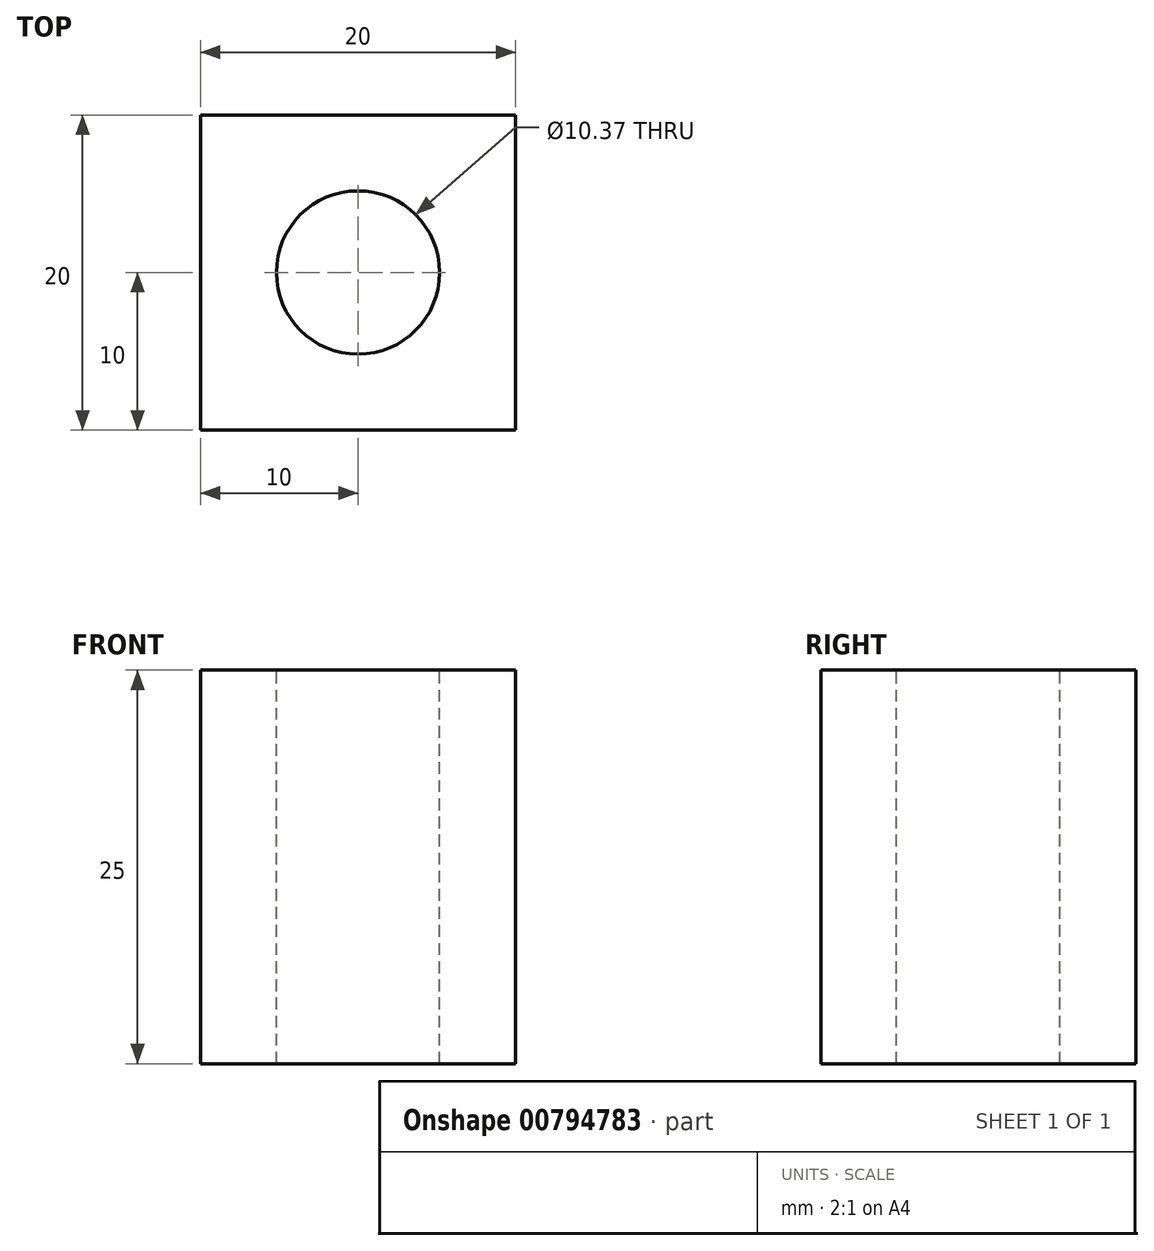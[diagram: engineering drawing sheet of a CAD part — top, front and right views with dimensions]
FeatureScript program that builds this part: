
annotation { "Feature Type Name" : "Feature", "Feature Type Description" : "" }
export const myFeature = defineFeature(function(context is Context, id is Id, definition is map)
    precondition{}
    {
        {
            var Q0;
            Q0=qCreatedBy(makeId("Top.planeOp"),FACE);
            var sketch = newSketch(context, id + "F0", { "sketchPlane" : qUnion([Q0])});
            skLineSegment(sketch, "E0.bottom", {"start": v(10, -10) * mm, "end": v(-10, -10) * mm});
            skLineSegment(sketch, "E0.top", {"start": v(10, 10) * mm, "end": v(-10, 10) * mm});
            skLineSegment(sketch, "E0.left", {"start": v(10, -10) * mm, "end": v(10, 10) * mm});
            skLineSegment(sketch, "E0.right", {"start": v(-10, -10) * mm, "end": v(-10, 10) * mm});
            skPoint(sketch, "E0.middle", {"position": v(0, 0) * mm});
            skSolve(sketch);
        }
        {
            var Q0;
            Q0 = qSketchRegion(id + "F0", true);
            extrude(context, id + "F1", {"entities" : qUnion([Q0]), "depth" : 25 * mm, "offsetDistance" : 25 * mm});
        }
        {
            var Q0;
            Q0=makeQuery(id+"F1.opExtrude","CAP_FACE",FACE,{"disambiguationData":[OSD([sQuery(id+"F0.wireOp",EDGE,"E0.bottom"),sQuery(id+"F0.wireOp",EDGE,"E0.top"),sQuery(id+"F0.wireOp",EDGE,"E0.left"),sQuery(id+"F0.wireOp",EDGE,"E0.right")])],"isStart":false});
            var sketch = newSketch(context, id + "F2", { "sketchPlane" : qUnion([Q0])});
            skSolve(sketch);
        }
        {
            var Q0;
            Q0=makeQuery(id+"F2.imprint","IMPRINT",FACE,{"disambiguationData":[TD([[makeQuery(id+"F2.imprint","IMPRINT",EDGE,{"derivedFrom":makeQuery(id+"F1.opExtrude","CAP_EDGE",EDGE,{"disambiguationData":[OSD([sQuery(id+"F0.wireOp",EDGE,"E0.bottom")])],"isStart":false})}),-1.0]])]});
            cPlane(context, id + "F3", {"entities" : qUnion([Q0]), "cplaneType" : CPlaneType.OFFSET, "offset" : 25 * mm, "width" : 150 * mm, "height" : 150 * mm});
        }
        {
            var Q0;
            Q0=qCreatedBy(id+"F3.planeOp",FACE);
            var sketch = newSketch(context, id + "F4", { "sketchPlane" : qUnion([Q0])});
            skCircle(sketch, "E1", {"center": v(0, 0) * mm, "radius": 5.19 * mm});
            skSolve(sketch);
        }
        {
            var Q0;
            Q0=makeQuery(id+"F4.imprint","IMPRINT",FACE,{"disambiguationData":[TD([[makeQuery(id+"F4.imprint","IMPRINT",EDGE,{"derivedFrom":sQuery(id+"F4.wireOp",EDGE,"E1")}),1.0]])]});
            extrude(context, id + "F5", {"entities" : qUnion([Q0]), "operationType" : NewBodyOperationType.REMOVE, "oppositeDirection" : true, "depth" : 100 * mm, "offsetDistance" : 25 * mm});
        }
    });
